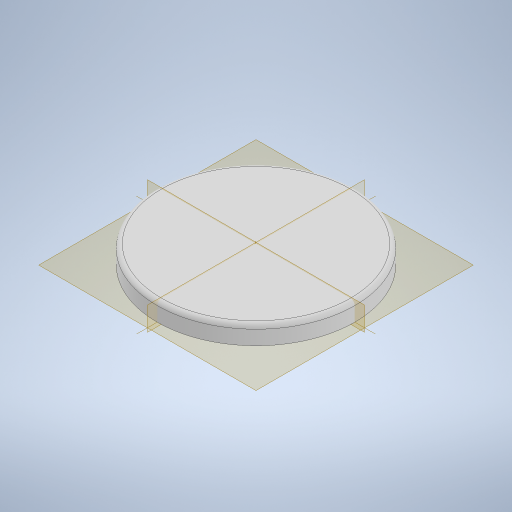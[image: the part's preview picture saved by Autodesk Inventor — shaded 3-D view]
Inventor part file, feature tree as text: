
AUTODESK INVENTOR PART (.ipt)
format: ipt  version: 2023 (Build 270158000, 158)  size: 586,240 bytes
history: native  units: in
note: dims shown in document units (in); Inventor stores cm internally (conversion verified against a paired STEP export)
features: extrude x6, sketch x6, fillet x1, chamfer x1
ambient origin geometry x8: Origin, YZ Plane, XZ Plane, XY Plane, X Axis, Y Axis, Z Axis, Center Point
bodies: Solid1 (feature_tree)
feature tree (14):
  extrude  "Extrusion1"  Depth=0.5118in TaperAngle=0.0deg
  extrude  "Extrusion2"  Depth=0.1181in TaperAngle=0.0deg
  extrude  "Extrusion3"  Depth=0.1969in TaperAngle=0.0deg
  extrude  "Extrusion4"  Depth=0.0787in TaperAngle=0.0deg
  extrude  "Extrusion5"  Depth=0.2756in
  fillet  "Fillet1"  Radius=0.315in
  chamfer  "Chamfer1"  Distance=0.0787in Angle=45.0deg
  extrude  "Extrusion6"  Depth=0.1378in
  sketch  "Sketch1"  dims[d0=5.4331in d1=0.5118in d2=0.0in]
  sketch  "Sketch2"  dims[d3=5.2362in d4=0.1181in d5=0.0in]
  sketch  "Sketch3"  dims[d6=5.0591in d7=0.1969in d8=0.0in]
  sketch  "Sketch4"  dims[d9=0.5906in d10=0.0787in d11=0.0in]
  sketch  "Sketch5"  dims[d12=0.2953in d13=0.2756in d14=0.315in d15=0.0in]
  sketch  "Sketch6"  dims[d16=0.1181in d17=0.0787in d18=0.0787in d19=45.0deg d20=0.1378in d21=0.0295in d23=23.622in d25=360.0deg d27=0.1969in d28=0.0in]
